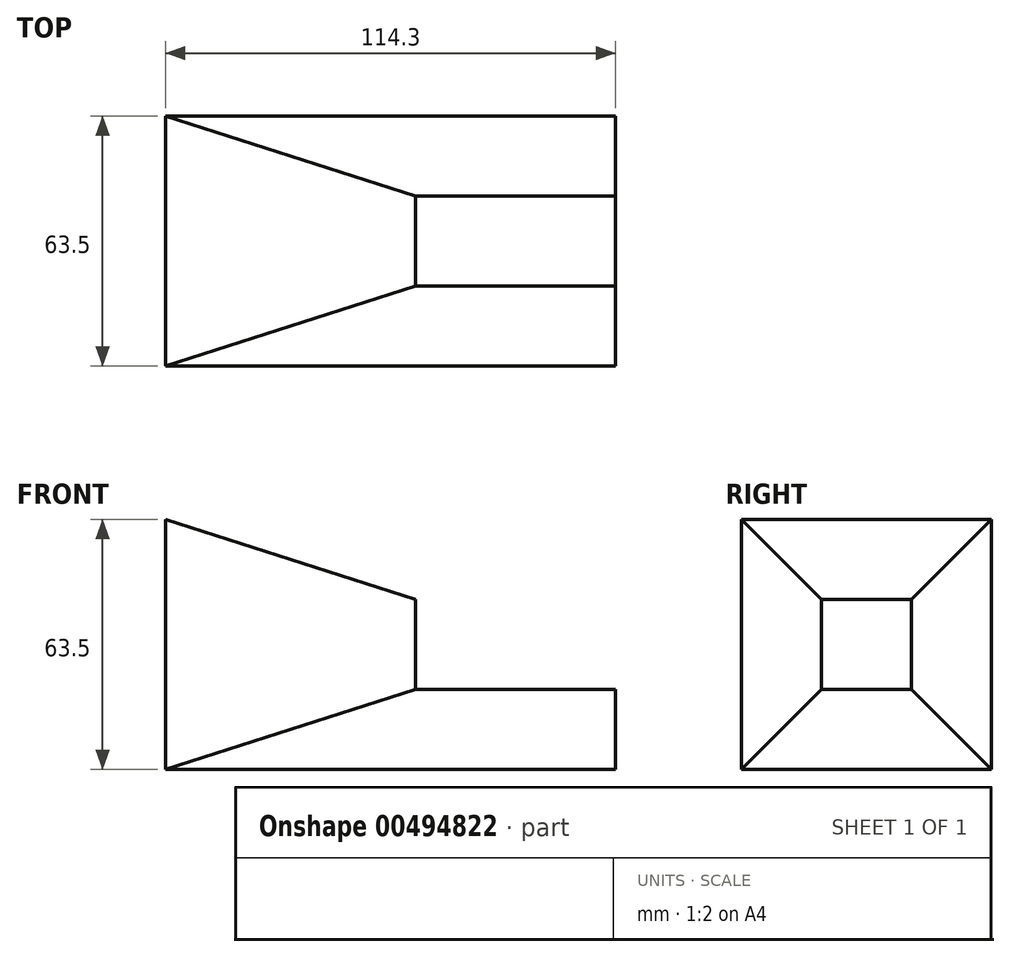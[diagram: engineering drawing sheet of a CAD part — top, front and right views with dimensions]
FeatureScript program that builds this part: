
annotation { "Feature Type Name" : "Feature", "Feature Type Description" : "" }
export const myFeature = defineFeature(function(context is Context, id is Id, definition is map)
    precondition{}
    {
        {
            var Q0;
            Q0=qCreatedBy(makeId("Right.planeOp"),FACE);
            var sketch = newSketch(context, id + "F0", { "sketchPlane" : qUnion([Q0])});
            skLineSegment(sketch, "E0.bottom", {"start": v(31.75, 31.75) * mm, "end": v(-31.75, 31.75) * mm});
            skLineSegment(sketch, "E0.top", {"start": v(31.75, -31.75) * mm, "end": v(-31.75, -31.75) * mm});
            skLineSegment(sketch, "E0.left", {"start": v(31.75, 31.75) * mm, "end": v(31.75, -31.75) * mm});
            skLineSegment(sketch, "E0.right", {"start": v(-31.75, 31.75) * mm, "end": v(-31.75, -31.75) * mm});
            skPoint(sketch, "E0.middle", {"position": v(0, 0) * mm});
            skSolve(sketch);
        }
        {
            var Q0;
            Q0 = qSketchRegion(id + "F0", true);
            extrude(context, id + "F1", {"entities" : qUnion([Q0]), "endBound" : BoundingType.SYMMETRIC, "depth" : 63.5 * mm});
        }
        {
            var Q0;
            Q0=makeQuery(id+"F1.opExtrude","CAP_EDGE",EDGE,{"disambiguationData":[OSD([sQuery(id+"F0.wireOp",EDGE,"E0.right")])],"isStart":false});
            var Q1;
            Q1=makeQuery(id+"F1.opExtrude","CAP_EDGE",EDGE,{"disambiguationData":[OSD([sQuery(id+"F0.wireOp",EDGE,"E0.bottom")])],"isStart":false});
            var Q2;
            Q2=makeQuery(id+"F1.opExtrude","CAP_EDGE",EDGE,{"disambiguationData":[OSD([sQuery(id+"F0.wireOp",EDGE,"E0.left")])],"isStart":false});
            var Q3;
            Q3=makeQuery(id+"F1.opExtrude","CAP_EDGE",EDGE,{"disambiguationData":[OSD([sQuery(id+"F0.wireOp",EDGE,"E0.top")])],"isStart":false});
            chamfer(context, id + "F2", {"entities" : qUnion([Q0, Q1, Q2, Q3]), "chamferType" : ChamferType.TWO_OFFSETS, "width1" : 20.32 * mm, "oppositeDirection" : false, "width2" : 63.5 * mm, "tangentPropagation" : true});
        }
        {
            var Q0;
            Q0=makeQuery(id+"F1.opExtrude","CAP_FACE",FACE,{"disambiguationData":[OSD([sQuery(id+"F0.wireOp",EDGE,"E0.bottom"),sQuery(id+"F0.wireOp",EDGE,"E0.top"),sQuery(id+"F0.wireOp",EDGE,"E0.left"),sQuery(id+"F0.wireOp",EDGE,"E0.right")])],"isStart":true});
            var sketch = newSketch(context, id + "F3", { "sketchPlane" : qUnion([Q0])});
            skLineSegment(sketch, "E1", {"start": v(31.75, -31.75) * mm, "end": v(-31.75, -31.75) * mm});
            skLineSegment(sketch, "E2", {"start": v(-31.75, -31.75) * mm, "end": v(-11.43, -11.43) * mm});
            skLineSegment(sketch, "E3", {"start": v(-11.43, -11.43) * mm, "end": v(11.43, -11.43) * mm});
            skLineSegment(sketch, "E4", {"start": v(11.43, -11.43) * mm, "end": v(31.75, -31.75) * mm});
            skSolve(sketch);
        }
        {
            var Q0;
            Q0 = qSketchRegion(id + "F3", true);
            extrude(context, id + "F4", {"entities" : qUnion([Q0]), "operationType" : NewBodyOperationType.ADD, "oppositeDirection" : true, "depth" : 114.3 * mm});
        }
    });
